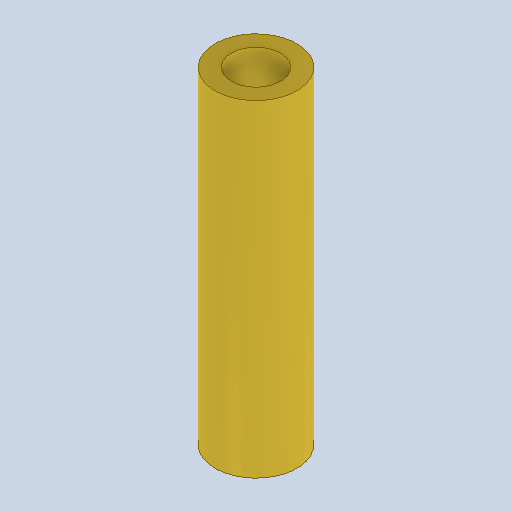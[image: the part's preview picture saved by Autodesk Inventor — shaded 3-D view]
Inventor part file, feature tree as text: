
AUTODESK INVENTOR PART (.ipt)
format: ipt  version: 2023 (Build 270158000, 158)  size: 85,504 bytes
history: native  units: in
note: dims shown in document units (in); Inventor stores cm internally (conversion verified against a paired STEP export)
features: other x3, sketch x1
ambient origin geometry x8: Origin, YZ Plane, XZ Plane, XY Plane, X Axis, Y Axis, Z Axis, Center Point
bodies: Solid1 (feature_tree)
feature tree (4):
  other  "Trudong30.ipt"
  other  "Solid1::Trudong30.ipt"
  other  "TaggingFeature1"
  sketch  "Sketch1"  dims[d0=0.3937in]
